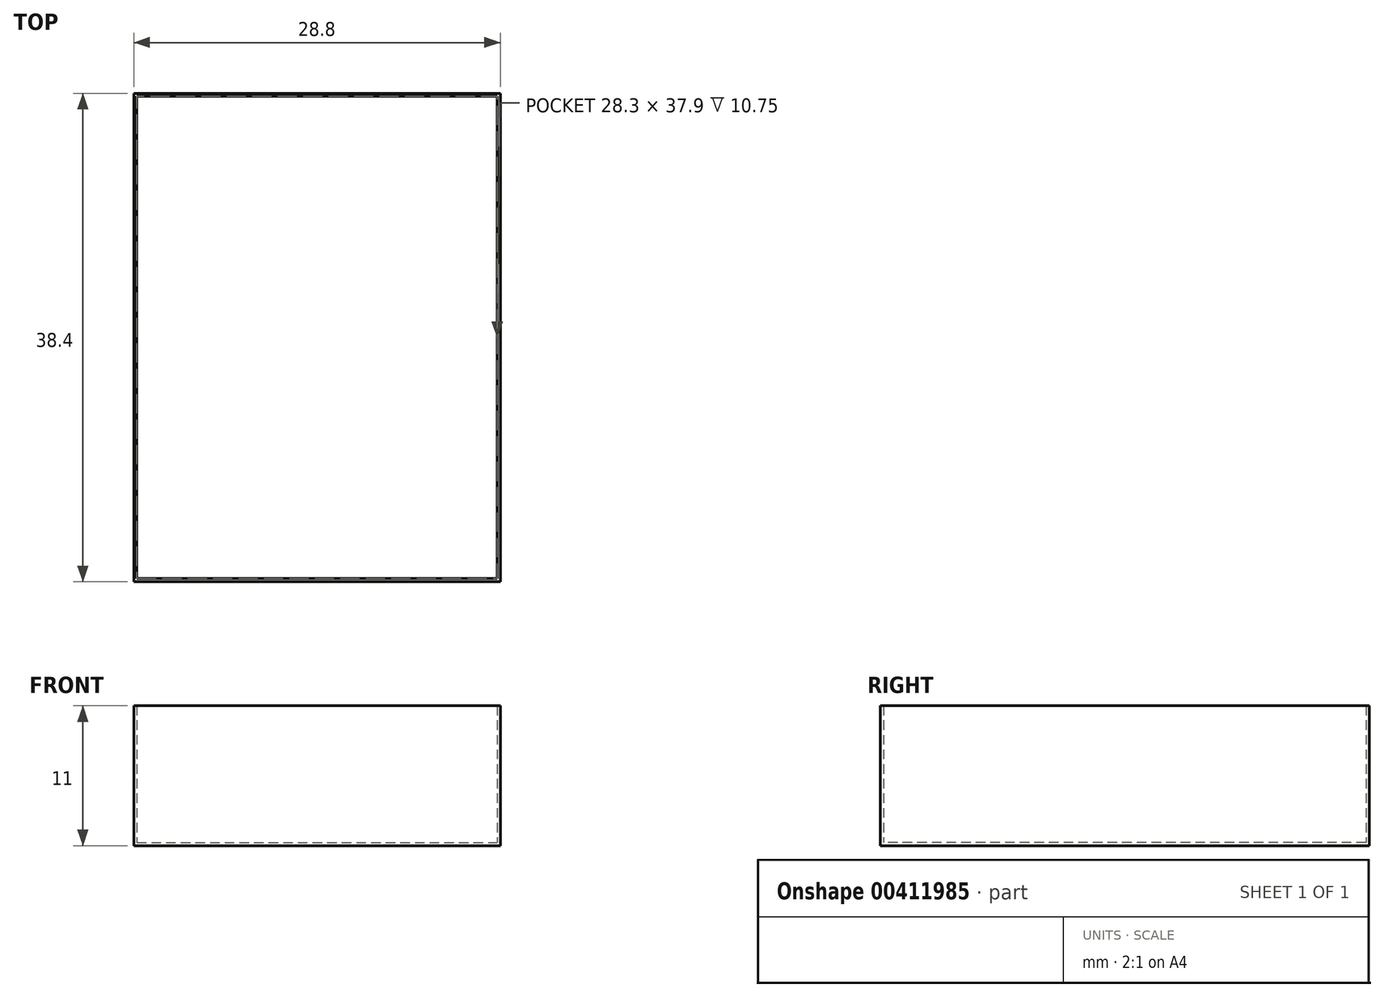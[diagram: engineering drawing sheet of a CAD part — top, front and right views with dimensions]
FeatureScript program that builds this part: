
annotation { "Feature Type Name" : "Feature", "Feature Type Description" : "" }
export const myFeature = defineFeature(function(context is Context, id is Id, definition is map)
    precondition{}
    {
        {
            var Q0;
            Q0=qCreatedBy(makeId("Top.planeOp"),FACE);
            var sketch = newSketch(context, id + "F0", { "sketchPlane" : qUnion([Q0])});
            skLineSegment(sketch, "E0", {"start": v(0, 0) * mm, "end": v(28.8, 0) * mm});
            skLineSegment(sketch, "E1", {"start": v(28.8, 0) * mm, "end": v(28.8, 38.4) * mm});
            skLineSegment(sketch, "E2", {"start": v(28.8, 38.4) * mm, "end": v(0, 38.4) * mm});
            skLineSegment(sketch, "E3", {"start": v(0, 38.4) * mm, "end": v(0, 0) * mm});
            skSolve(sketch);
        }
        {
            var Q0;
            Q0 = qSketchRegion(id + "F0", true);
            extrude(context, id + "F1", {"entities" : qUnion([Q0]), "depth" : 11 * mm});
        }
        {
            var Q0;
            Q0=makeQuery(id+"F1.opExtrude","CAP_FACE",FACE,{"disambiguationData":[OSD([sQuery(id+"F0.wireOp",EDGE,"E0"),sQuery(id+"F0.wireOp",EDGE,"E1"),sQuery(id+"F0.wireOp",EDGE,"E2"),sQuery(id+"F0.wireOp",EDGE,"E3")])],"isStart":false});
            shell(context, id + "F2", {"entities" : qUnion([Q0]), "thickness" : 0.25 * mm});
        }
        {
            var Q0;
            Q0=makeQuery(id+"F2.opShell","OFFSET_FACE",FACE,{"disambiguationData":[OSD([sQuery(id+"F0.wireOp",EDGE,"E0"),sQuery(id+"F0.wireOp",EDGE,"E1"),sQuery(id+"F0.wireOp",EDGE,"E2"),sQuery(id+"F0.wireOp",EDGE,"E3")])]});
            var sketch = newSketch(context, id + "F3", { "sketchPlane" : qUnion([Q0])});
            skLineSegment(sketch, "E4", {"start": v(14.4, 0.25) * mm, "end": v(14.4, 7.25) * mm});
            skLineSegment(sketch, "E5", {"start": v(14.4, 7.25) * mm, "end": v(3.4, 7.25) * mm});
            skSolve(sketch);
        }
        {
            var Q0;
            Q0=sQuery(id+"F3.wireOp",EDGE,"E5");
            var Q1;
            Q1=sQuery(id+"F3.wireOp",EDGE,"E4");
            extrude(context, id + "F4", {"bodyType" : ToolBodyType.SURFACE, "surfaceEntities" : qUnion([Q0, Q1]), "depth" : 11 * mm});
        }
        {
            var Q0;
            Q0=makeQuery(id+"F2.opShell","OFFSET_FACE",FACE,{"disambiguationData":[OSD([sQuery(id+"F0.wireOp",EDGE,"E0"),sQuery(id+"F0.wireOp",EDGE,"E1"),sQuery(id+"F0.wireOp",EDGE,"E2"),sQuery(id+"F0.wireOp",EDGE,"E3")])]});
            var sketch = newSketch(context, id + "F5", { "sketchPlane" : qUnion([Q0])});
            skLineSegment(sketch, "E6", {"start": v(28.55, 11.85) * mm, "end": v(16.5, 11.85) * mm});
            skLineSegment(sketch, "E7", {"start": v(16.5, 11.85) * mm, "end": v(16.5, 22.82) * mm});
            skLineSegment(sketch, "E8", {"start": v(16.5, 22.82) * mm, "end": v(28.55, 22.82) * mm});
            skSolve(sketch);
        }
        {
            var Q0;
            Q0 = qSketchRegion(id + "F5", true);
            var Q1;
            Q1=sQuery(id+"F5.wireOp",EDGE,"E7");
            var Q2;
            Q2=sQuery(id+"F5.wireOp",EDGE,"E6");
            var Q3;
            Q3=sQuery(id+"F5.wireOp",EDGE,"E8");
            extrude(context, id + "F6", {"entities" : qUnion([Q0]), "bodyType" : ToolBodyType.SURFACE, "surfaceEntities" : qUnion([Q1, Q2, Q3]), "depth" : 11 * mm});
        }
    });
